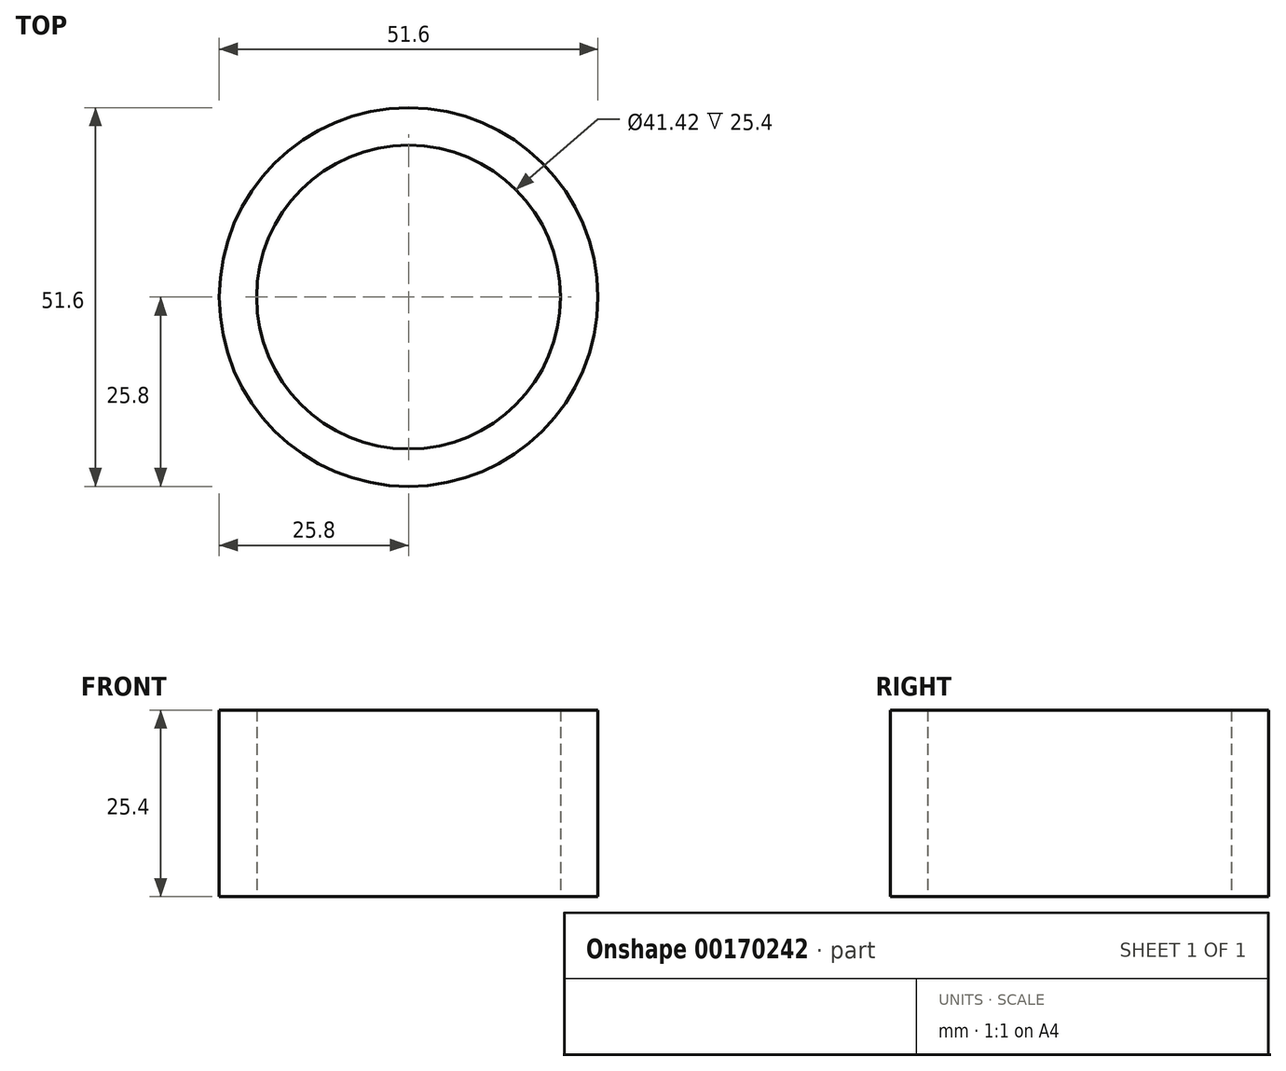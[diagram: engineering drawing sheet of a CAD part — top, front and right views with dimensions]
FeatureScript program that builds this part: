
annotation { "Feature Type Name" : "Feature", "Feature Type Description" : "" }
export const myFeature = defineFeature(function(context is Context, id is Id, definition is map)
    precondition{}
    {
        {
            var Q0;
            Q0=qCreatedBy(makeId("Top.planeOp"),FACE);
            var sketch = newSketch(context, id + "F0", { "sketchPlane" : qUnion([Q0])});
            skCircle(sketch, "E0", {"center": v(0, 0) * mm, "radius": 25.8 * mm});
            skLineSegment(sketch, "E1", {"start": v(0, 38.17) * mm, "end": v(0, -42.74) * mm, "construction": true});
            skSolve(sketch);
        }
        {
            var Q0;
            Q0=makeQuery(id+"F0.imprint","IMPRINT",FACE,{"disambiguationData":[TD([[makeQuery(id+"F0.imprint","IMPRINT",EDGE,{"derivedFrom":sQuery(id+"F0.wireOp",EDGE,"E0")}),1.0]])]});
            extrude(context, id + "F1", {"entities" : qUnion([Q0]), "depth" : 25.4 * mm});
        }
        {
            var Q0;
            Q0=qCreatedBy(makeId("Top.planeOp"),FACE);
            var sketch = newSketch(context, id + "F2", { "sketchPlane" : qUnion([Q0])});
            skCircle(sketch, "E2", {"center": v(0, 0) * mm, "radius": 20.7 * mm});
            skLineSegment(sketch, "E3", {"start": v(0, 44.07) * mm, "end": v(0, -48.52) * mm, "construction": true});
            skSolve(sketch);
        }
        {
            var Q0;
            Q0=makeQuery(id+"F2.imprint","IMPRINT",FACE,{"disambiguationData":[TD([[makeQuery(id+"F2.imprint","IMPRINT",EDGE,{"derivedFrom":sQuery(id+"F2.wireOp",EDGE,"E2")}),1.0]])]});
            extrude(context, id + "F3", {"entities" : qUnion([Q0]), "operationType" : NewBodyOperationType.REMOVE, "endBound" : BoundingType.THROUGH_ALL, "depth" : 25.4 * mm});
        }
    });
